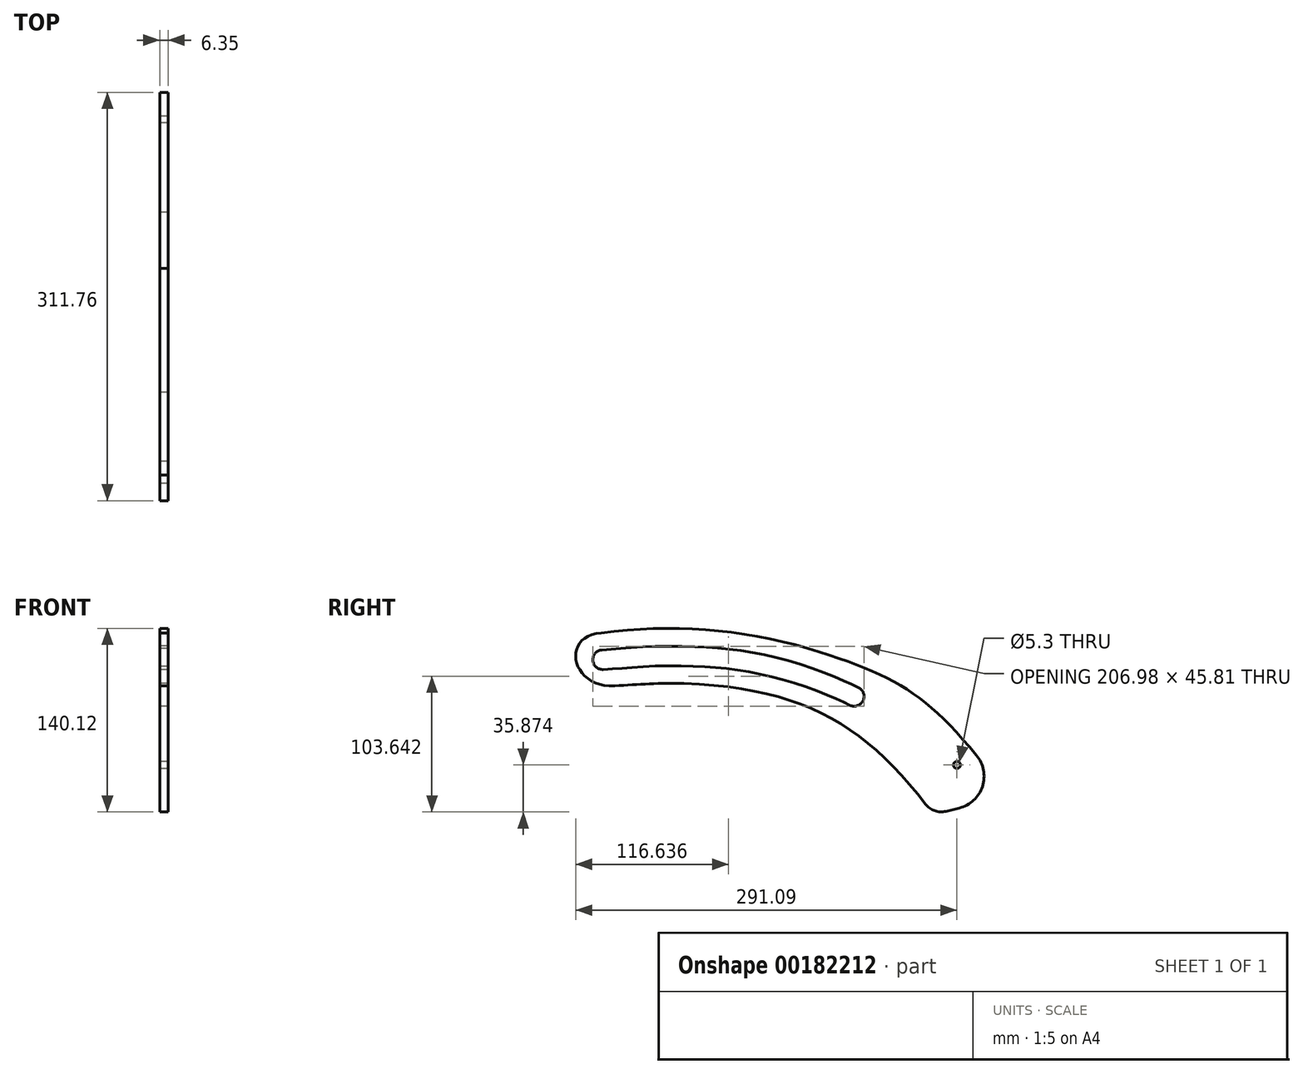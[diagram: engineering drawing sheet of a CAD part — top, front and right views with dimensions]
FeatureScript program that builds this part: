
annotation { "Feature Type Name" : "Feature", "Feature Type Description" : "" }
export const myFeature = defineFeature(function(context is Context, id is Id, definition is map)
    precondition{}
    {
        {
            var Q0;
            Q0=qCreatedBy(makeId("Right.planeOp"),FACE);
            var sketch = newSketch(context, id + "F0", { "sketchPlane" : qUnion([Q0])});
            skFitSpline(sketch, "E0", {"points": [v(0, 0) * mm, v(192, -28) * mm], "startDerivative": vector(187.7, 13.1) * mm, "endDerivative": vector(228.7, -105.68) * mm, "construction": true});
            skArc(sketch, "E1.0.startCap", {"start": v(0.52, -7.48) * mm, "mid": v(-7.48, -0.52) * mm, "end": v(-0.52, 7.48) * mm});
            skArc(sketch, "E1.0.endCap", {"start": v(195.15, -21.2) * mm, "mid": v(198.8, -31.15) * mm, "end": v(188.85, -34.8) * mm});
            skFitSpline(sketch, "E1.0.left", {"points": [v(-0.52, 7.48) * mm, v(15.14, 8.57) * mm, v(37.9, 10.09) * mm, v(68.32, 10.09) * mm, v(91.52, 8.63) * mm, v(115.44, 5.26) * mm, v(140.41, -0.46) * mm, v(166.75, -8.94) * mm, v(185.45, -16.71) * mm, v(195.15, -21.2) * mm]});
            skFitSpline(sketch, "E1.0.right", {"points": [v(0.52, -7.48) * mm, v(16.15, -6.4) * mm, v(38.55, -4.91) * mm, v(67.89, -4.92) * mm, v(90.02, -6.31) * mm, v(112.71, -9.51) * mm, v(136.4, -14.93) * mm, v(161.52, -23.02) * mm, v(179.5, -30.48) * mm, v(188.85, -34.8) * mm]});
            skLineSegment(sketch, "E2", {"start": v(272.13, -113.28) * mm, "end": v(261.95, -115.8) * mm});
            skFitSpline(sketch, "E3", {"points": [v(252.35, -118.17) * mm, v(62.1, -18.03) * mm], "startDerivative": vector(-147.57, 199.4) * mm, "endDerivative": vector(-284.66, 11.89) * mm});
            skFitSpline(sketch, "E4", {"points": [v(156.76, 8.69) * mm, v(310.04, -103.92) * mm], "startDerivative": vector(229.69, -71.81) * mm, "endDerivative": vector(178.63, -230.1) * mm});
            skArc(sketch, "E5.filletArc", {"start": v(246.48, -110.4) * mm, "mid": v(253.4, -115.4) * mm, "end": v(261.95, -115.8) * mm});
            skArc(sketch, "E6.filletArc", {"start": v(272.13, -113.28) * mm, "mid": v(289.89, -96.8) * mm, "end": v(285.33, -73) * mm});
            skFitSpline(sketch, "E7", {"points": [v(9.37, -20.06) * mm, v(-1.08, 20.47) * mm], "startDerivative": vector(-100.53, -5.96) * mm, "endDerivative": vector(93.66, 6.16) * mm});
            skFitSpline(sketch, "E8", {"points": [v(1.43, -20.47) * mm, v(9.23, -19.92) * mm, v(24.4, -18.9) * mm, v(46.22, -17.93) * mm, v(67.5, -17.94) * mm, v(88.71, -19.28) * mm, v(110.34, -22.33) * mm, v(132.92, -27.5) * mm, v(156.98, -35.24) * mm, v(174.32, -42.43) * mm, v(183.4, -46.63) * mm], "construction": true});
            skArc(sketch, "E9", {"start": v(156.76, 8.69) * mm, "mid": v(78.45, 22.83) * mm, "end": v(-1.08, 20.47) * mm});
            skArc(sketch, "E10", {"start": v(62.1, -18.03) * mm, "mid": v(35.72, -18.45) * mm, "end": v(9.37, -20.06) * mm});
            skPoint(sketch, "E11", {"position": v(270.46, -80.36) * mm});
            skCircle(sketch, "E12", {"center": v(270.46, -80.36) * mm, "radius": 2.65 * mm});
            skSolve(sketch);
        }
        {
            var Q0;
            Q0=qSketchRegion(id+"F0",true);
            extrude(context, id + "F1", {"entities" : qUnion([Q0]), "depth" : 6.35 * mm});
        }
    });
